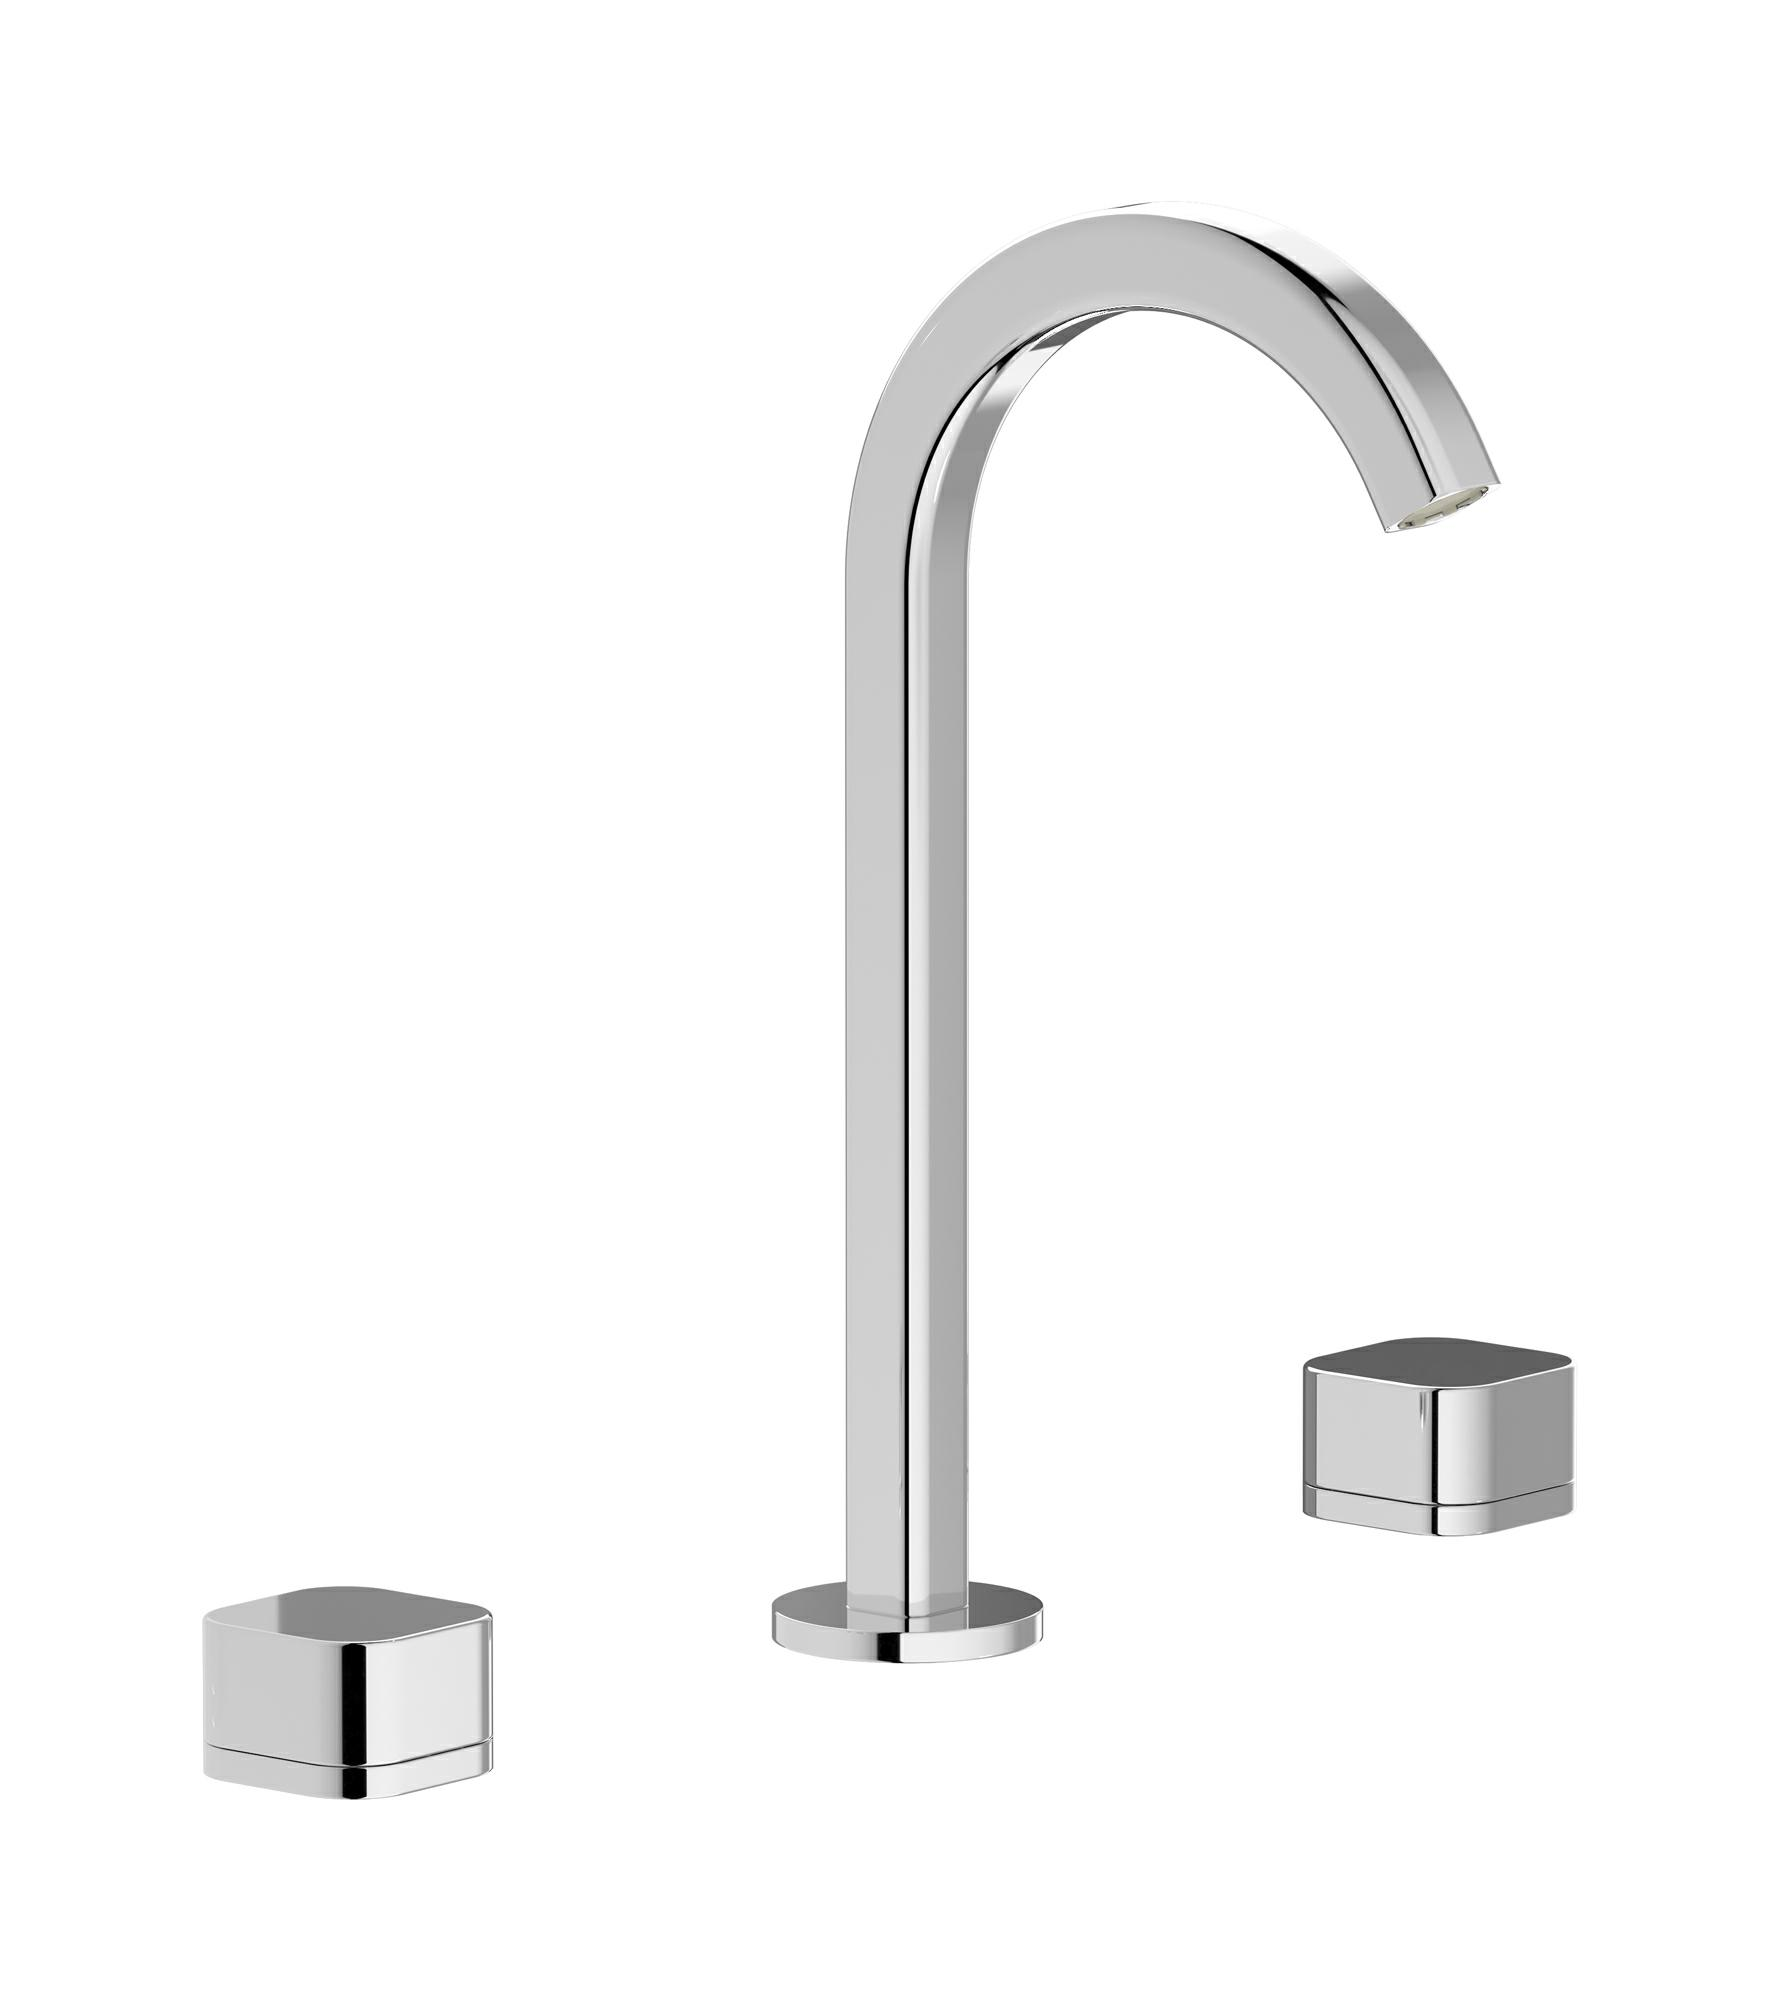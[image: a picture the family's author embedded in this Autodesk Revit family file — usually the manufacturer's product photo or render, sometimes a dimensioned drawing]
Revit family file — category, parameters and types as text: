
# Revit family: EO392_1
name_source: partatom
category: Apparecchi idraulici
units: mm (PartAtom-declared; Revit-internal decimal feet)

## family parameters
Basato su piano di lavoro = No
Condiviso = No
Mantieni orientamento annotazione = No
Numero OmniClass = 23.45.55.17
Punto di calcolo locali = No
Quota connettore circolare = Usa diametro
Sempre verticale = Sì
Taglio con vuoti quando caricato = No
Tipo di parte = Normale
Titolo OmniClass = Mixing Faucets

## types (12) — shared parameters
Cold water inlet = 10 mm  [stored 0.0328084 ft]
Commenti sul tipo = Washbasin
Connessione CW = No
Connessione HW = No
Connessione di scarico = No
Connessione di ventilazione = No
Descrizione = Three hole washbasin complete
Hot water inlet = 10 mm  [stored 0.0328084 ft]
Produttore = IB Rubinetterie S.p.A.
URL = https://www.weareib.it
zero-valued in all types: Prospetto di default

## per-type parameters (varying)
| type | Finishes surface | Immagine tipo | Modello |
| Chrome | IB_Chrome | EO392CC_1.jpg | EO392CC_1 |
| Brushed nickel | IB_Brushed nickel | EO392SS_1.jpg | EO392SS_1 |
| Natural brass | IB_Brass | EO392ON_1.jpg | EO392ON_1 |
| Matt black | IB_matt black | EO392NP_1.jpg | EO392NP_1 |
| Black chrome | IB_Black chrome | EO392CF_1.jpg | EO392CF_1 |
| Brushed black chrome | IB_Brushed black chrome | EO392CS_1.jpg | EO392CS_1 |
| Pale gold | IB_Pale gold | EO392II_1.jpg | EO392II_1 |
| Brushed pale gold | IB_brushed pale gold | EO392IS_1.jpg | EO392IS_1 |
| Rose gold | IB_Rose gold | EO392RS_1.jpg | EO392RS_1 |
| Brushed rose gold | IB_Brushed rose gold | EO392SR_1.jpg | EO392SR_1 |
| Gold | IB_gold | EO392OO_1.jpg | EO392OO_1 |
| Brushed gold | IB_brushed gold | EO392OS_1.jpg | EO392OS_1 |

note: [stored X ft] marks values corroborated as IEEE doubles in the binary element streams (Revit-internal decimal feet)
